# Revit family: Gira_011600
name_source: partatom
category: Allgemeines Modell
revit_build: Autodesk Revit 2017 (Build: 20160225_1515(x64)
units: mm (PartAtom-declared; Revit-internal decimal feet)

## family parameters
Basisbauteil = Fläche
Beim Laden mit Abzugskörper schneiden = Nein
Bemaßung runder Anschluss = Durchmesser verwenden
Gemeinsam genutzt = Nein
Kann Basisbauteil für Bewehrung sein = Nein
Raumberechnungspunkt = Nein
Teiletyp = Normal

## types (1)
- Gira_011600
    App control via Bluetooth = Nein
    Applicable with button = Ja
    Applicable with infrared button = Nein
    Applicable with movement sensor = Nein
    Applicable with presence indicator = Nein
    Applicable with time switch/timer = Nein
    Applicable with transmission button = Nein
    Assembly arrangement = Basic element
    BIM = https://media.stage.bim.site
    Beschreibung = Rock.ind.sw.off 2-w Ins.,Rocker indicator switch insert 10 AX 250 V~ with neon lamp element 230 V,,Universal off 2-way switch,Notes :,- Can also be connected with illumination.
    Colour = Other
    Connection type = Plug clamp
    Data sheet = https://katalog.gira.de
    Dimming phase cut-off = Nein
    Dimming phase cut-on = Nein
    Frequency [Hz] = [50:60]
    Function lighting = Illuminated (on)
    GTIN = 4010337116004
    HAN = 011600
    Halogen free = Nein
    Hersteller = Gira
    Illumination = Yes
    Label space/information surface 1 = No
    Light value memory = Nein
    Material = Other
    Material quality = Other
    Method of operation = Rocker/button
    Mounting method = Flush mounted (plaster)
    Nominal voltage [Volt] = 250
    Nominal voltage [Volt] 1 = [230:230]
    Number of modules (module system) = 1
    Number of rockers = 1
    Productwebsite = http://katalog.gira.de
    Push button switch = Nein
    Rated current = 10 A
    Serial dimmer = Nein
    Substation input = Nein
    Suitable for degree of protection (IP) = IP20
    Surface protection = Other
    Transparent = Nein
    Type of fastening = Mounting with claw and screw
    Type of lighting = Glow lamp
    Type of load = Other
    Typname = Rock.ind.sw. off/2-way Insert
    URL = https://www.gira.de
    Vorgabe-Ansicht = 1219 mm
    Washing machine switch = Nein
    Wiring system = Two-way switch
    With mounting plate = Nein

## geometry (parser evidence)
native form markers: Sweep x2
no freeform markers — native parametric forms only
